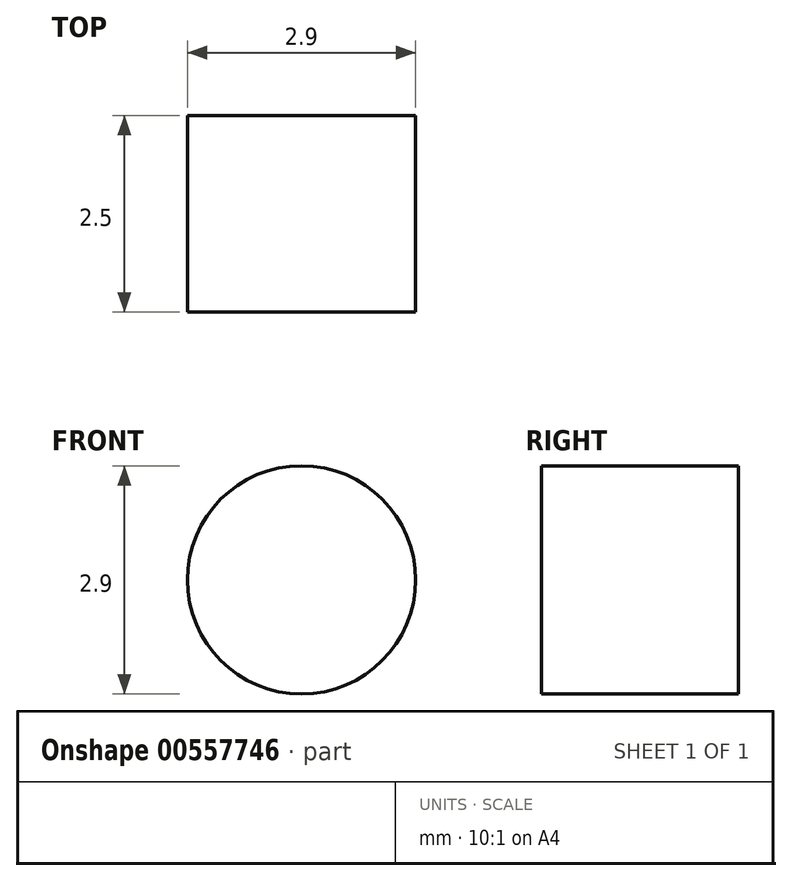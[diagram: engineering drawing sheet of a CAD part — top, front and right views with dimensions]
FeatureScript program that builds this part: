
annotation { "Feature Type Name" : "Feature", "Feature Type Description" : "" }
export const myFeature = defineFeature(function(context is Context, id is Id, definition is map)
    precondition{}
    {
        {
            var Q0;
            Q0=qCreatedBy(makeId("Front.planeOp"),FACE);
            var sketch = newSketch(context, id + "F0", { "sketchPlane" : qUnion([Q0])});
            skLineSegment(sketch, "E0.bottom", {"start": v(20, 6) * mm, "end": v(-20, 6) * mm});
            skLineSegment(sketch, "E0.top", {"start": v(20, -6) * mm, "end": v(-20, -6) * mm});
            skLineSegment(sketch, "E0.left", {"start": v(20, 6) * mm, "end": v(20, -6) * mm});
            skLineSegment(sketch, "E0.right", {"start": v(-20, 6) * mm, "end": v(-20, -6) * mm});
            skPoint(sketch, "E0.middle", {"position": v(0, 0) * mm});
            skSolve(sketch);
        }
        {
            var Q0;
            Q0=makeQuery(id+"F0.imprint","IMPRINT",FACE,{"disambiguationData":[TD([[makeQuery(id+"F0.imprint","IMPRINT",EDGE,{"derivedFrom":sQuery(id+"F0.wireOp",EDGE,"E0.bottom")}),1.0]])]});
            extrude(context, id + "F1", {"entities" : qUnion([Q0]), "depth" : 2.5 * mm, "offsetDistance" : 25 * mm});
        }
        {
            var Q0;
            Q0=makeQuery(id+"F1.opExtrude","CAP_FACE",FACE,{"disambiguationData":[OSD([sQuery(id+"F0.wireOp",EDGE,"E0.bottom"),sQuery(id+"F0.wireOp",EDGE,"E0.top"),sQuery(id+"F0.wireOp",EDGE,"E0.left"),sQuery(id+"F0.wireOp",EDGE,"E0.right")])],"isStart":false});
            var sketch = newSketch(context, id + "F2", { "sketchPlane" : qUnion([Q0])});
            skCircle(sketch, "E1", {"center": v(-16, 2.5) * mm, "radius": 1.45 * mm});
            skCircle(sketch, "E2.MirrorC", {"center": v(16, 2.5) * mm, "radius": 1.45 * mm});
            skSolve(sketch);
        }
        {
            var Q0;
            Q0=makeQuery(id+"F2.imprint","IMPRINT",FACE,{"disambiguationData":[TD([[makeQuery(id+"F2.imprint","IMPRINT",EDGE,{"derivedFrom":sQuery(id+"F2.wireOp",EDGE,"E1")}),1.0]])]});
            var Q1;
            Q1=makeQuery(id+"F2.imprint","IMPRINT",FACE,{"disambiguationData":[TD([[makeQuery(id+"F2.imprint","IMPRINT",EDGE,{"derivedFrom":sQuery(id+"F2.wireOp",EDGE,"E2.MirrorC")}),-1.0]])]});
            extrude(context, id + "F3", {"entities" : qUnion([Q0, Q1]), "operationType" : NewBodyOperationType.REMOVE, "endBound" : BoundingType.UP_TO_NEXT, "oppositeDirection" : true, "depth" : 25 * mm, "offsetDistance" : 25 * mm});
        }
    });
